# Revit family: Deca_Ducha Higiênica Belle Epoque Tradicional_1984.C52.ACT_Registro e Derivação
name_source: partatom
category: Plumbing Fixtures
revit_build: Autodesk Revit Architecture 2012 (Build: 20120126_0600(x64)
units: mm (PartAtom-declared; Revit-internal decimal feet)

## types (2) — shared parameters
Aprovado por = Contino/quattroD
Assembly Code = D2010700
Atendimento ao Cliente = 0800-0117073
Consumo = Varia com a pressão
Criado por = Contino/quattroD
Description = Ducha higiênica com registro e derivação
Diâmetro Água Fria = 15 mm  [stored 0.0492126 ft]
Ducha Higiênica = Deca CR10 Cromado Metal
Flow Pressure = 0.00 psi
Informações Complementares = Mecanismo: 3 1/2 voltas
Linha = Belle Epoque Tradicional
Louça/Metais = Metal
Manufacturer = Deca
Material = Deca_Latão Cromado e Plástico de Engenharia
Norma = ABNT NBR 14877:2002
Peso Liquido (Kg) = 1
Pressão = 2 A 40 mca
Produto = Ducha higiênica com registro e derivação Belle Epoque Tradicional
Raio Água Fria = 8 mm  [stored 0.0262467 ft]
Segmento = Competitivo
URL = www.deca.com.br/produtos
Variações de COR = Cromado (1984.C52.ACT); Cromado com dourado (1984.C52.ACT.DO)
zero-valued in all types: CWFU

## per-type parameters (varying)
| type | Código | Default Elevation | Detalhes | Model |
| 1984.C52.ACT_Cromado CR10 | 1984.C52.ACT | 800 mm  [stored 2.62467 ft] | Deca CR10 Cromado Metal | 1984.C52.ACT |
| 1984.C52.ACT.DO_Dourado DR11 | 1984.C52.ACT.DO | 0 mm  [stored 0 ft] | Deca DR11 Dourado Metal | 1984.C52.ACT.DO |

note: [stored X ft] marks values corroborated as IEEE doubles in the binary element streams (Revit-internal decimal feet)

## geometry (parser evidence)
native form markers: Blend x4, Sweep x2
no freeform markers — native parametric forms only
